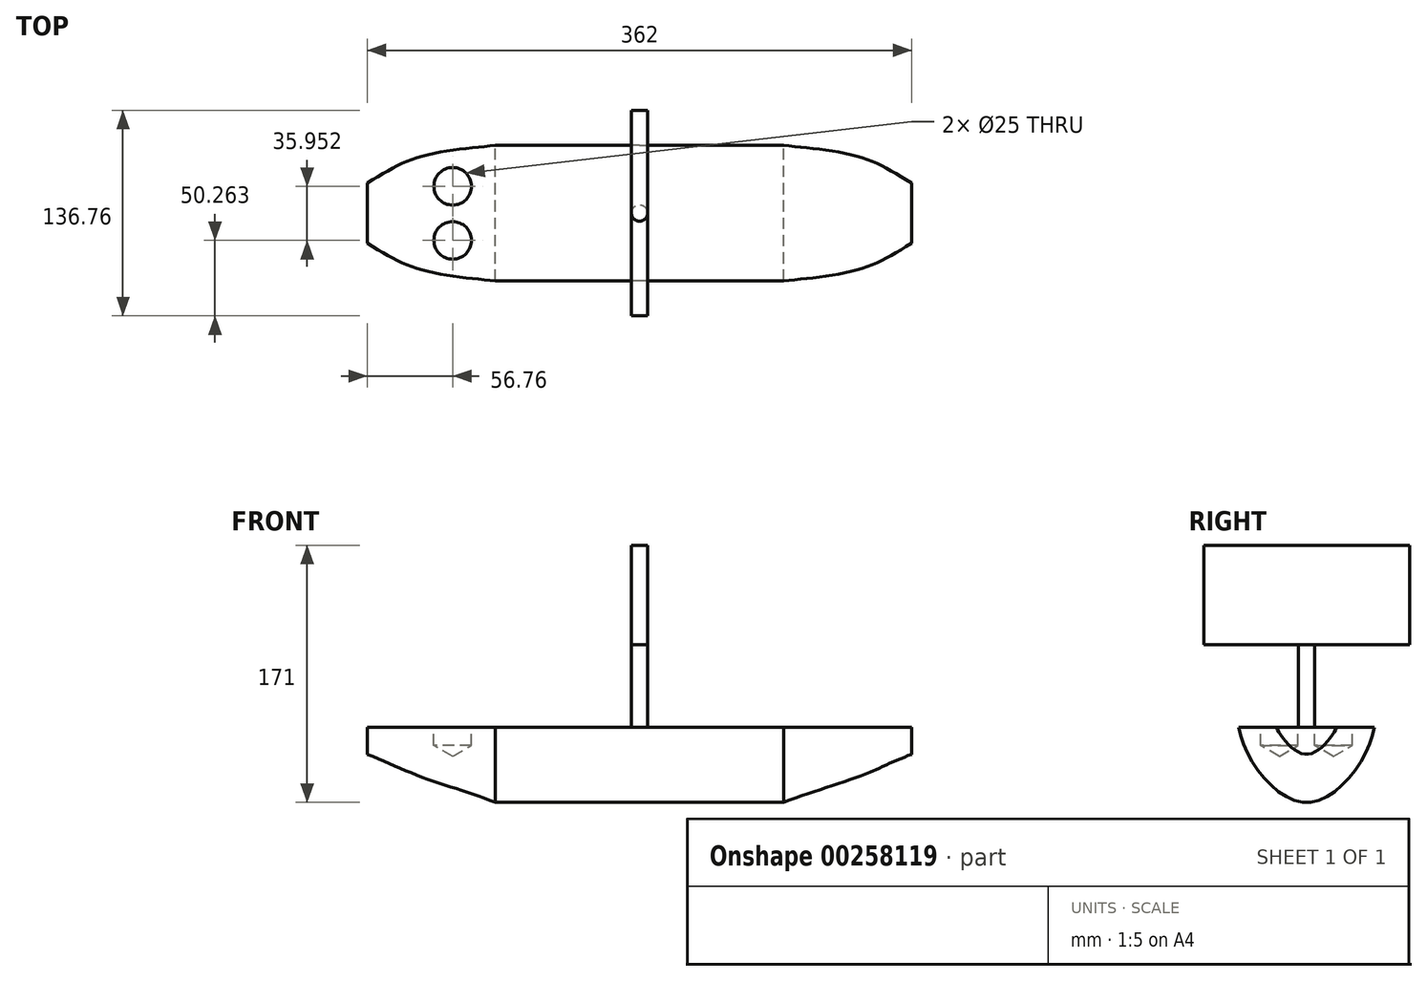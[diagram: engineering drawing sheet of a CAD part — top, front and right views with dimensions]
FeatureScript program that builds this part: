
annotation { "Feature Type Name" : "Feature", "Feature Type Description" : "" }
export const myFeature = defineFeature(function(context is Context, id is Id, definition is map)
    precondition{}
    {
        {
            var Q0;
            Q0=qCreatedBy(makeId("Right.planeOp"),FACE);
            cPlane(context, id + "F0", {"entities" : qUnion([Q0]), "cplaneType" : CPlaneType.OFFSET, "offset" : 85 * mm, "oppositeDirection" : true, "width" : 150 * mm, "height" : 150 * mm});
        }
        {
            var Q0;
            Q0=qCreatedBy(makeId("Right.planeOp"),FACE);
            var sketch = newSketch(context, id + "F1", { "sketchPlane" : qUnion([Q0])});
            skFitSpline(sketch, "E0", {"points": [v(-45, 0) * mm, v(0, -50) * mm, v(45, 0) * mm], "startDerivative": vector(18, -120) * mm, "endDerivative": vector(18, 120) * mm});
            skLineSegment(sketch, "E1", {"start": v(45, 0) * mm, "end": v(-45, 0) * mm});
            skSolve(sketch);
        }
        {
            var Q0;
            Q0=qCreatedBy(id+"F0.planeOp",FACE);
            var sketch = newSketch(context, id + "F2", { "sketchPlane" : qUnion([Q0])});
            skFitSpline(sketch, "E2", {"points": [v(20, 0) * mm, v(0, -18) * mm, v(-20, 0) * mm], "startDerivative": vector(-12, -30) * mm, "endDerivative": vector(-12, 30) * mm});
            skLineSegment(sketch, "E3", {"start": v(20, 0) * mm, "end": v(-20, 0) * mm});
            skSolve(sketch);
        }
        {
            var Q0;
            Q0=qCreatedBy(makeId("Top.planeOp"),FACE);
            var sketch = newSketch(context, id + "F3", { "sketchPlane" : qUnion([Q0])});
            skFitSpline(sketch, "E4", {"points": [v(0, -45) * mm, v(-48.67, -37.8) * mm, v(-85, -20) * mm], "startDerivative": vector(-75.94, 7.5) * mm, "endDerivative": vector(-86.16, 52.2) * mm});
            skLineSegment(sketch, "E5", {"start": v(0, 0) * mm, "end": v(-80.4, 0) * mm, "construction": true});
            skFitSpline(sketch, "E6.MirrorCS", {"points": [v(0, 45) * mm, v(-48.67, 37.8) * mm, v(-85, 20) * mm], "startDerivative": vector(-75.94, -7.5) * mm, "endDerivative": vector(-86.16, -52.2) * mm});
            skSolve(sketch);
        }
        {
            var Q0;
            Q0=makeQuery(id+"F1.imprint","IMPRINT",FACE,{"disambiguationData":[TD([[makeQuery(id+"F1.imprint","IMPRINT",EDGE,{"derivedFrom":sQuery(id+"F1.wireOp",EDGE,"E0")}),1.0]])]});
            var Q1;
            Q1=makeQuery(id+"F2.imprint","IMPRINT",FACE,{"disambiguationData":[TD([[makeQuery(id+"F2.imprint","IMPRINT",EDGE,{"derivedFrom":sQuery(id+"F2.wireOp",EDGE,"E2")}),-1.0]])]});
            var Q2;
            Q2=sQuery(id+"F3.wireOp",EDGE,"E4");
            var Q3;
            Q3=sQuery(id+"F3.wireOp",EDGE,"E6.MirrorCS");
            loft(context, id + "F4", {"addGuides" : true, "sheetProfilesArray" : [{ "sheetProfileEntities" : qUnion([Q0]) }, { "sheetProfileEntities" : qUnion([Q1]) }], "guidesArray" : [{ "guideEntities" : qUnion([Q2]), "guideDerivativeType" : LoftGuideDerivativeType.DEFAULT, "guideDerivativeMagnitude" : 1 }, { "guideEntities" : qUnion([Q3]), "guideDerivativeType" : LoftGuideDerivativeType.DEFAULT, "guideDerivativeMagnitude" : 1 }]});
        }
        {
            var Q0;
            Q0=makeQuery(id+"F4.opLoft","CAP_FACE",FACE,{"disambiguationData":[OSD([makeQuery(id+"F1.imprint","IMPRINT",FACE,{"disambiguationData":[TD([[makeQuery(id+"F1.imprint","IMPRINT",EDGE,{"derivedFrom":sQuery(id+"F1.wireOp",EDGE,"E0")}),1.0]])]})])],"isStart":true});
            extrude(context, id + "F5", {"entities" : qUnion([Q0]), "operationType" : NewBodyOperationType.ADD, "depth" : 96 * mm});
        }
        {
            var Q0;
            {var subQ0=sQuery(id+"F3.wireOp",EDGE,"E6.MirrorCS");var subQ1=sQuery(id+"F3.wireOp",EDGE,"E4");var subQ2=sQuery(id+"F1.wireOp",EDGE,"E1");Q0=makeQuery(id+"F5.boolean.opBoolean","MERGE",FACE,{"derivedFrom":[makeQuery(id+"F4.opLoft","SWEPT_FACE",FACE,{"disambiguationData":[OSD([sQuery(id+"F1.wireOp",EDGE,"E0"),subQ2,sQuery(id+"F2.wireOp",EDGE,"E2"),sQuery(id+"F2.wireOp",EDGE,"E3"),subQ1,subQ0])]}),makeQuery(id+"F5.opExtrude","SWEPT_FACE",FACE,{"disambiguationData":[OSD([subQ2,subQ1,subQ0])]})]});}
            var sketch = newSketch(context, id + "F6", { "sketchPlane" : qUnion([Q0])});
            skPoint(sketch, "E7", {"position": v(-28.24, 17.83) * mm});
            skPoint(sketch, "E8", {"position": v(-28.24, -18.12) * mm});
            skSolve(sketch);
        }
        {
            var Q0;
            Q0=makeQuery(id+"F4.opLoft","SWEPT_BODY",BODY,{"disambiguationData":[OSD([makeQuery(id+"F1.imprint","IMPRINT",FACE,{"disambiguationData":[TD([[makeQuery(id+"F1.imprint","IMPRINT",EDGE,{"derivedFrom":sQuery(id+"F1.wireOp",EDGE,"E0")}),1.0]])]}),makeQuery(id+"F2.imprint","IMPRINT",FACE,{"disambiguationData":[TD([[makeQuery(id+"F2.imprint","IMPRINT",EDGE,{"derivedFrom":sQuery(id+"F2.wireOp",EDGE,"E2")}),-1.0]])]}),sQuery(id+"F3.wireOp",EDGE,"E4"),sQuery(id+"F3.wireOp",EDGE,"E6.MirrorCS")])]});
            var Q1;
            Q1=makeQuery(id+"F5.opExtrude","CAP_FACE",FACE,{"disambiguationData":[OSD([makeQuery(id+"F1.imprint","IMPRINT",FACE,{"disambiguationData":[TD([[makeQuery(id+"F1.imprint","IMPRINT",EDGE,{"derivedFrom":sQuery(id+"F1.wireOp",EDGE,"E0")}),1.0]])]})])],"isStart":false});
            mirror(context, id + "F7", {"operationType" : NewBodyOperationType.ADD, "entities" : qUnion([Q0]), "mirrorPlane" : qUnion([Q1])});
        }
        {
            var Q0;
            {var subQ0=sQuery(id+"F3.wireOp",EDGE,"E6.MirrorCS");var subQ1=sQuery(id+"F3.wireOp",EDGE,"E4");var subQ2=sQuery(id+"F1.wireOp",EDGE,"E1");var subQ3=makeQuery(id+"F5.boolean.opBoolean","MERGE",FACE,{"derivedFrom":[makeQuery(id+"F4.opLoft","SWEPT_FACE",FACE,{"disambiguationData":[OSD([sQuery(id+"F1.wireOp",EDGE,"E0"),subQ2,sQuery(id+"F2.wireOp",EDGE,"E2"),sQuery(id+"F2.wireOp",EDGE,"E3"),subQ1,subQ0])]}),makeQuery(id+"F5.opExtrude","SWEPT_FACE",FACE,{"disambiguationData":[OSD([subQ2,subQ1,subQ0])]})]});Q0=makeQuery(id+"F7.boolean.opBoolean","MERGE",FACE,{"derivedFrom":[subQ3,makeQuery(id+"F7.opPattern","COPY",FACE,{"derivedFrom":subQ3,"instanceName":"1"})]});}
            var sketch = newSketch(context, id + "F8", { "sketchPlane" : qUnion([Q0])});
            skLineSegment(sketch, "E9", {"start": v(96, 45) * mm, "end": v(96, -45) * mm});
            skLineSegment(sketch, "E10", {"start": v(-85, 0) * mm, "end": v(277, 0) * mm});
            skCircle(sketch, "E11", {"center": v(96, 0) * mm, "radius": 5.35 * mm});
            skSolve(sketch);
        }
        {
            var Q0;
            Q0 = qSketchRegion(id + "F8", true);
            extrude(context, id + "F9", {"entities" : qUnion([Q0]), "operationType" : NewBodyOperationType.ADD, "depth" : 55 * mm});
        }
        {
            var Q0;
            Q0=makeQuery(id+"F9.opExtrude","CAP_FACE",FACE,{"disambiguationData":[OSD([sQuery(id+"F8.wireOp",EDGE,"E11")])],"isStart":false});
            var sketch = newSketch(context, id + "F10", { "sketchPlane" : qUnion([Q0])});
            skLineSegment(sketch, "E12.top", {"start": v(90.65, 68.38) * mm, "end": v(101.35, 68.38) * mm});
            skLineSegment(sketch, "E12.left", {"start": v(90.65, 0) * mm, "end": v(90.65, 68.38) * mm});
            skLineSegment(sketch, "E12.right", {"start": v(101.35, 0) * mm, "end": v(101.35, 68.38) * mm});
            skLineSegment(sketch, "E13.MirrorCS", {"start": v(90.65, 0) * mm, "end": v(90.65, -68.38) * mm});
            skLineSegment(sketch, "E14.MirrorCS", {"start": v(101.35, 0) * mm, "end": v(101.35, -68.38) * mm});
            skLineSegment(sketch, "E15.MirrorCS", {"start": v(90.65, -68.38) * mm, "end": v(101.35, -68.38) * mm});
            skSolve(sketch);
        }
        {
            var Q0;
            Q0=makeQuery(id+"F10.imprint","IMPRINT",FACE,{"disambiguationData":[TD([[makeQuery(id+"F10.imprint","IMPRINT",EDGE,{"derivedFrom":sQuery(id+"F10.wireOp",EDGE,"E12.top")}),-1.0]])]});
            var Q1;
            {var subQ0=sQuery(id+"F10.wireOp",EDGE,"E13.MirrorCS");Q1=makeQuery(id+"F10.imprint","IMPRINT",FACE,{"disambiguationData":[TD([[makeQuery(id+"F10.imprint","IMPRINT",EDGE,{"derivedFrom":subQ0}),1.0]])]});}
            var Q2;
            {var subQ0=makeQuery(id+"F9.opExtrude","CAP_EDGE",EDGE,{"disambiguationData":[OSD([sQuery(id+"F8.wireOp",EDGE,"E11")])],"isStart":false});var subQ1=makeQuery(id+"F10.imprint","INTERSECT",VERTEX,{"derivedFrom":[subQ0,sQuery(id+"F10.wireOp",EDGE,"E12.left"),sQuery(id+"F10.wireOp",EDGE,"E13.MirrorCS")]});Q2=makeQuery(id+"F10.imprint","IMPRINT",FACE,{"disambiguationData":[TD([[makeQuery(id+"F10.imprint","IMPRINT",EDGE,{"disambiguationData":[TD([[subQ1,1.0]])],"derivedFrom":subQ0}),1.0]])]});}
            extrude(context, id + "F11", {"entities" : qUnion([Q0, Q1, Q2]), "operationType" : NewBodyOperationType.ADD, "depth" : 66 * mm});
        }
        {
            var Q0;
            Q0=sQuery(id+"F6.wireOp",VERTEX,"E7");
            var Q1;
            Q1=sQuery(id+"F6.wireOp",VERTEX,"E8");
            var Q2;
            Q2=makeQuery(id+"F4.opLoft","SWEPT_BODY",BODY,{"disambiguationData":[OSD([makeQuery(id+"F1.imprint","IMPRINT",FACE,{"disambiguationData":[TD([[makeQuery(id+"F1.imprint","IMPRINT",EDGE,{"derivedFrom":sQuery(id+"F1.wireOp",EDGE,"E0")}),1.0]])]}),makeQuery(id+"F2.imprint","IMPRINT",FACE,{"disambiguationData":[TD([[makeQuery(id+"F2.imprint","IMPRINT",EDGE,{"derivedFrom":sQuery(id+"F2.wireOp",EDGE,"E2")}),-1.0]])]}),sQuery(id+"F3.wireOp",EDGE,"E4"),sQuery(id+"F3.wireOp",EDGE,"E6.MirrorCS")])]});
            hole(context, id + "F12", {"style" : HoleStyle.SIMPLE, "endStyle" : HoleEndStyle.BLIND, "holeDiameter" : 25 * mm, "holeDepth" : 12 * mm, "tappedDepth" : 12 * mm, "tapClearance" : 3, "locations" : qUnion([Q0, Q1]), "scope" : qUnion([Q2])});
        }
    });
